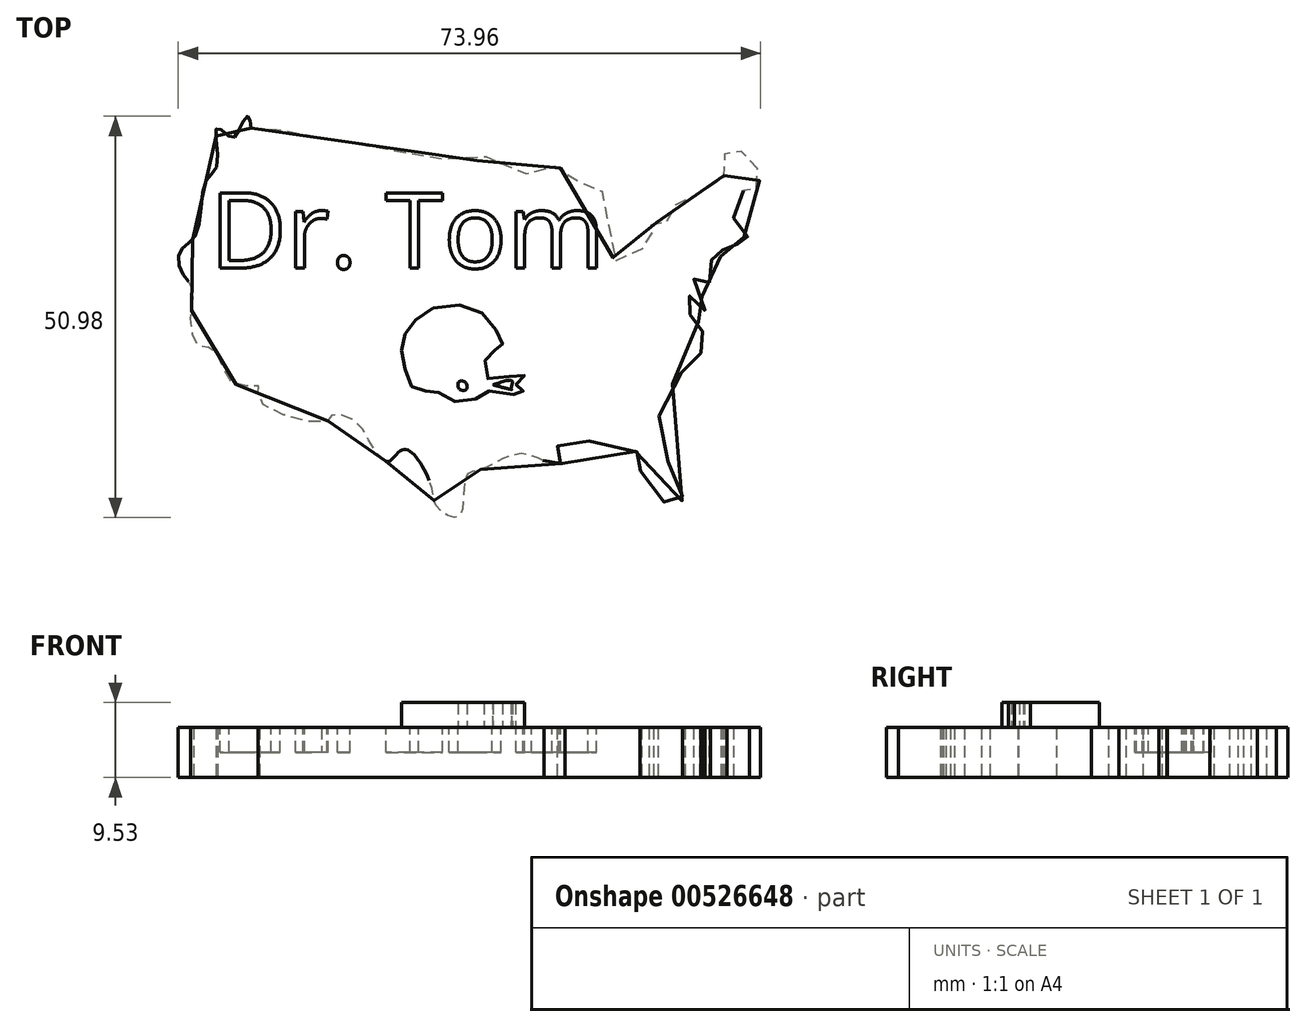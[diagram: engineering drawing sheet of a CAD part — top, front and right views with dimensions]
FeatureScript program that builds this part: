
annotation { "Feature Type Name" : "Feature", "Feature Type Description" : "" }
export const myFeature = defineFeature(function(context is Context, id is Id, definition is map)
    precondition{}
    {
        {
            var Q0;
            Q0=qCreatedBy(makeId("Top.planeOp"),FACE);
            var sketch = newSketch(context, id + "F0", { "sketchPlane" : qUnion([Q0])});
            skFitSpline(sketch, "E0", {"points": [v(-37.18, 0) * mm, v(-36.2, 0) * mm, v(-7.83, -4) * mm, v(-6.97, -3.25) * mm, v(-3.62, -5.85) * mm, v(1.2, -4.86) * mm, v(5.3, -7.34) * mm, v(7.77, -8.58) * mm, v(9, -16.75) * mm, v(13.22, -14.64) * mm, v(13.84, -13.28) * mm, v(13.34, -13.16) * mm, v(13.6, -12.41) * mm, v(14.2, -12.04) * mm, v(16.07, -11.67) * mm, v(17.18, -9.2) * mm, v(22.63, -6.97) * mm, v(22.63, -4.36) * mm, v(24.12, -2.38) * mm, v(26.1, -4.24) * mm, v(27.5, -5.97) * mm, v(26.1, -8.45) * mm, v(25.35, -7.96) * mm, v(24.24, -9.94) * mm, v(24.86, -13.78) * mm, v(26.1, -13.9) * mm, v(25.23, -14.9) * mm, v(23.87, -14.52) * mm, v(22.5, -15.26) * mm, v(23.25, -16) * mm, v(21.14, -16.87) * mm, v(21.14, -18.73) * mm, v(20.53, -19.97) * mm, v(19.04, -19.1) * mm, v(20.4, -22.44) * mm, v(20.15, -23.44) * mm, v(18.42, -21.33) * mm, v(17.92, -22.7) * mm, v(19.29, -24.3) * mm, v(20.15, -25.54) * mm, v(19.78, -27.27) * mm, v(19.9, -28.76) * mm, v(18.05, -30.5) * mm, v(14.46, -37.68) * mm, v(16.93, -44.74) * mm, v(17.43, -47.58) * mm, v(15.57, -47.7) * mm, v(12.23, -43.5) * mm, v(12.35, -41.76) * mm, v(10.25, -40.65) * mm, v(1.7, -39.9) * mm, v(2.45, -41.64) * mm, v(2.45, -42.63) * mm, v(0, -42.01) * mm, v(0, -42.26) * mm, v(-2.63, -41.4) * mm, v(-7.96, -43.37) * mm, v(-9.94, -44.36) * mm, v(-10.8, -49.35) * mm, v(-13.53, -48.2) * mm, v(-14.15, -46.22) * mm, v(-16.5, -41.52) * mm, v(-18.24, -41.02) * mm, v(-19.85, -42.38) * mm, v(-22.2, -39.78) * mm, v(-23.93, -37.3) * mm, v(-26.9, -36.44) * mm, v(-27.52, -37.3) * mm, v(-36.2, -34.58) * mm, v(-36.2, -32.85) * mm, v(-39.41, -32.48) * mm, v(-41.89, -28.14) * mm, v(-43.75, -27.77) * mm, v(-44.86, -23.93) * mm, v(-44.61, -20.34) * mm, v(-46.12, -18.23) * mm, v(-46.12, -15.5) * mm, v(-44.24, -13.65) * mm, v(-43, -6.84) * mm, v(-41.52, -4.74) * mm, v(-41.52, 0) * mm, v(-39.66, -1.27) * mm, v(-38.67, 0) * mm, v(-37.55, 1.45) * mm, v(-37.18, 0) * mm]});
            skSolve(sketch);
        }
        {
            var Q0;
            Q0 = qSketchRegion(id + "F0", true);
            extrude(context, id + "F1", {"entities" : qUnion([Q0]), "depth" : 6.35 * mm, "offsetDistance" : 25.4 * mm});
        }
        {
            var Q0;
            Q0=makeQuery(id+"F1.opExtrude","CAP_FACE",FACE,{"disambiguationData":[OSD([sQuery(id+"F0.wireOp",EDGE,"E0")])],"isStart":false});
            var sketch = newSketch(context, id + "F2", { "sketchPlane" : qUnion([Q0])});
            skText(sketch, "E1", { "text": "Dr. Tom", "fontName": "OpenSans-Regular.ttf"});
            const initialGuessF2  = {"E1": [-0.04243, -0.0178, 1, 0, 0.00963]};
            skSetInitialGuess(sketch, initialGuessF2);
            skSolve(sketch);
        }
        {
            var Q0;
            Q0 = qSketchRegion(id + "F2", true);
            extrude(context, id + "F3", {"entities" : qUnion([Q0]), "operationType" : NewBodyOperationType.REMOVE, "oppositeDirection" : true, "depth" : 3.17 * mm, "offsetDistance" : 25.4 * mm});
        }
        {
            var Q0;
            {var subQ0=sQuery(id+"F0.wireOp",EDGE,"E0");Q0=makeQuery(id+"F3.boolean.opBoolean","SPLIT",FACE,{"disambiguationData":[TD([makeQuery(id+"F1.opExtrude","SWEPT_FACE",FACE,{"disambiguationData":[OSD([subQ0])]})])],"derivedFrom":makeQuery(id+"F1.opExtrude","CAP_FACE",FACE,{"disambiguationData":[OSD([subQ0])],"isStart":false})});}
            var sketch = newSketch(context, id + "F4", { "sketchPlane" : qUnion([Q0])});
            skFitSpline(sketch, "E2", {"points": [v(-17.62, -26.18) * mm, v(-16.85, -24.99) * mm, v(-15.66, -23.78) * mm, v(-13.25, -22.64) * mm, v(-9.73, -22.65) * mm, v(-7.5, -23.82) * mm, v(-6.09, -25.72) * mm, v(-5.53, -27.16) * mm, v(-5.24, -27.58) * mm, v(-5.51, -28.05) * mm, v(-6.12, -28.16) * mm, v(-7, -28.75) * mm, v(-7.53, -29.75) * mm, v(-7.34, -31.67) * mm, v(-6.07, -31.92) * mm, v(-3.4, -31.34) * mm, v(-2.55, -31.32) * mm, v(-2.55, -31.7) * mm, v(-3.2, -31.9) * mm, v(-3.55, -33.23) * mm, v(-3.22, -33.27) * mm, v(-2.55, -33.53) * mm, v(-2.55, -33.91) * mm, v(-4.66, -33.72) * mm, v(-7.2, -33.46) * mm, v(-8, -34) * mm, v(-9.75, -34.79) * mm, v(-11.83, -34.55) * mm, v(-13.25, -33.7) * mm, v(-13.87, -33.43) * mm, v(-14.9, -33.4) * mm, v(-16.21, -33.63) * mm, v(-17.1, -32.14) * mm, v(-17.6, -30.74) * mm, v(-18.01, -29.3) * mm, v(-18.01, -27.32) * mm, v(-17.62, -26.18) * mm]});
            skFitSpline(sketch, "E3", {"points": [v(-10.48, -32.12) * mm, v(-10.9, -32.42) * mm, v(-10.73, -33.23) * mm, v(-9.9, -33.23) * mm, v(-9.86, -32.49) * mm, v(-10.48, -32.12) * mm]});
            skFitSpline(sketch, "E4", {"points": [v(-6.48, -32.64) * mm, v(-4.16, -33.23) * mm, v(-4.08, -33.23) * mm, v(-6.48, -32.64) * mm]});
            skFitSpline(sketch, "E5", {"points": [v(-6.48, -32.64) * mm, v(-4.1, -32.11) * mm, v(-4.08, -32.64) * mm, v(-4.16, -33.23) * mm, v(-4.08, -33.23) * mm], "startDerivative": vector(6.82, 2.3) * mm, "endDerivative": vector(1.2, 0.38) * mm});
            skSolve(sketch);
        }
        {
            var Q0;
            Q0 = qSketchRegion(id + "F4", true);
            extrude(context, id + "F5", {"entities" : qUnion([Q0]), "operationType" : NewBodyOperationType.ADD, "depth" : 3.17 * mm, "offsetDistance" : 25.4 * mm});
        }
    });
